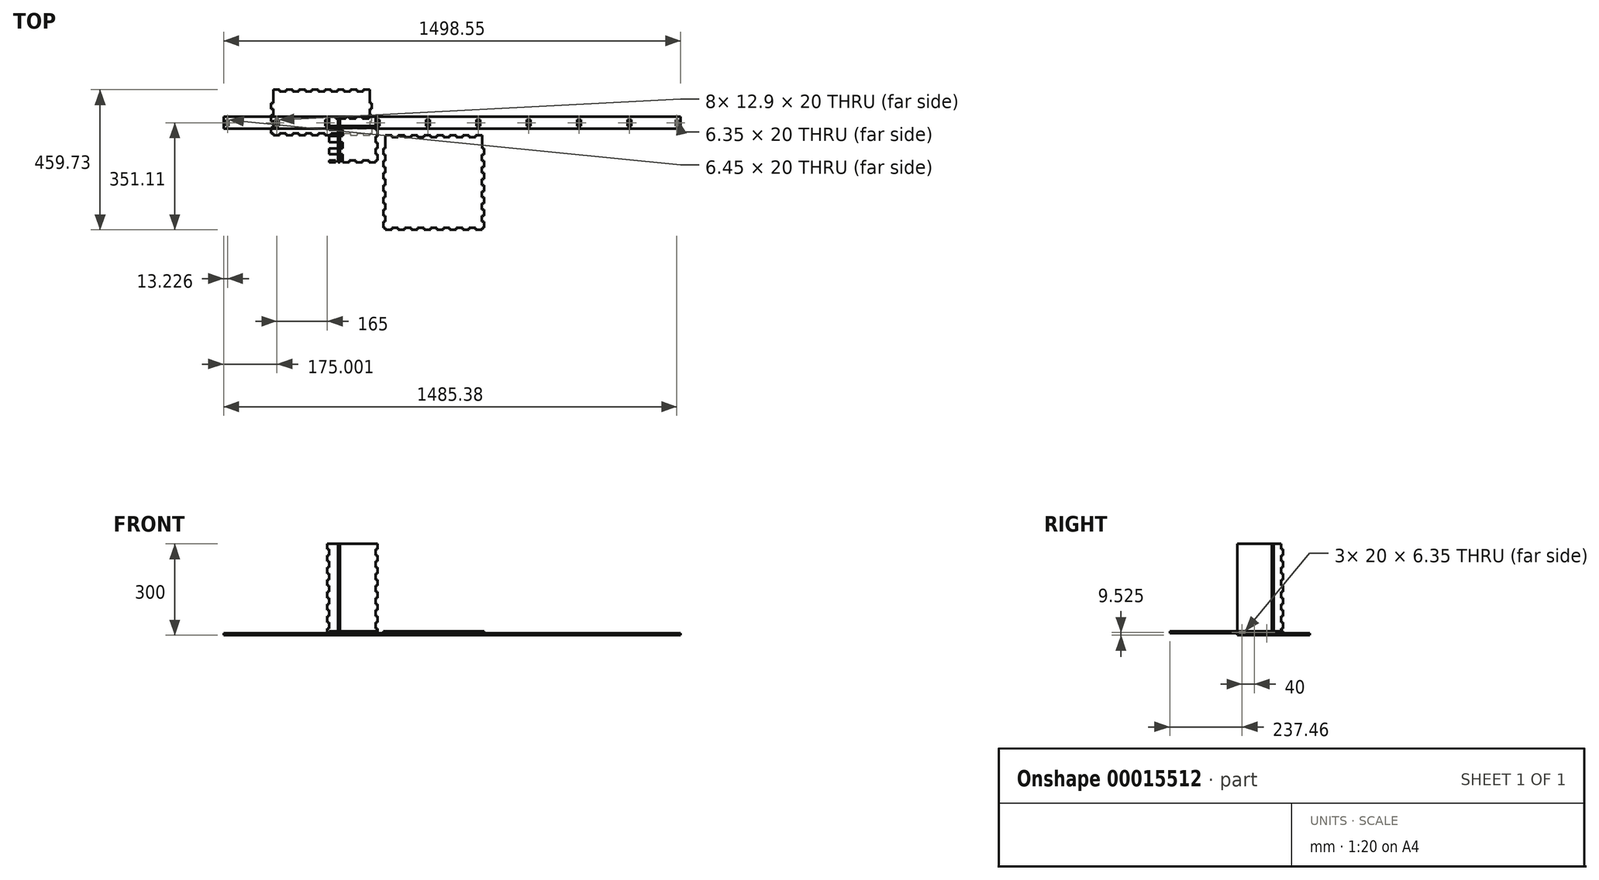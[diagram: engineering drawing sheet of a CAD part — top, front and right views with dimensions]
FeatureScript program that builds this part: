
annotation { "Feature Type Name" : "Feature", "Feature Type Description" : "" }
export const myFeature = defineFeature(function(context is Context, id is Id, definition is map)
    precondition{}
    {
        {
            var Q0;
            Q0=qCreatedBy(makeId("Top.planeOp"),FACE);
            var sketch = newSketch(context, id + "F0", { "sketchPlane" : qUnion([Q0])});
            skLineSegment(sketch, "E0.bottom", {"start": v(-375.58, 30) * mm, "end": v(1122.97, 30) * mm});
            skLineSegment(sketch, "E0.top", {"start": v(-375.58, -10) * mm, "end": v(1122.97, -10) * mm});
            skLineSegment(sketch, "E0.left", {"start": v(-375.58, 30) * mm, "end": v(-375.58, -10) * mm});
            skLineSegment(sketch, "E0.right", {"start": v(1122.97, 30) * mm, "end": v(1122.97, -10) * mm});
            skLineSegment(sketch, "E1.bottom", {"start": v(-207.03, 20) * mm, "end": v(-194.13, 20) * mm});
            skLineSegment(sketch, "E1.top", {"start": v(-207.03, 0) * mm, "end": v(-194.13, 0) * mm});
            skLineSegment(sketch, "E1.left", {"start": v(-207.03, 20) * mm, "end": v(-207.03, 0) * mm});
            skLineSegment(sketch, "E1.right", {"start": v(-194.13, 20) * mm, "end": v(-194.13, 0) * mm});
            skLineSegment(sketch, "E2.1.0.0", {"start": v(-29.13, 20) * mm, "end": v(-29.13, 0) * mm});
            skLineSegment(sketch, "E2.1.0.1", {"start": v(-42.03, 0) * mm, "end": v(-29.13, 0) * mm});
            skLineSegment(sketch, "E2.1.0.2", {"start": v(-42.03, 20) * mm, "end": v(-42.03, 0) * mm});
            skLineSegment(sketch, "E2.1.0.3", {"start": v(-42.03, 20) * mm, "end": v(-29.13, 20) * mm});
            skLineSegment(sketch, "E2.2.0.0", {"start": v(135.87, 20) * mm, "end": v(135.87, 0) * mm});
            skLineSegment(sketch, "E2.2.0.1", {"start": v(122.97, 0) * mm, "end": v(135.87, 0) * mm});
            skLineSegment(sketch, "E2.2.0.2", {"start": v(122.97, 20) * mm, "end": v(122.97, 0) * mm});
            skLineSegment(sketch, "E2.2.0.3", {"start": v(122.97, 20) * mm, "end": v(135.87, 20) * mm});
            skLineSegment(sketch, "E2.3.0.0", {"start": v(300.87, 20) * mm, "end": v(300.87, 0) * mm});
            skLineSegment(sketch, "E2.3.0.1", {"start": v(287.97, 0) * mm, "end": v(300.87, 0) * mm});
            skLineSegment(sketch, "E2.3.0.2", {"start": v(287.97, 20) * mm, "end": v(287.97, 0) * mm});
            skLineSegment(sketch, "E2.3.0.3", {"start": v(287.97, 20) * mm, "end": v(300.87, 20) * mm});
            skLineSegment(sketch, "E2.4.0.0", {"start": v(465.87, 20) * mm, "end": v(465.87, 0) * mm});
            skLineSegment(sketch, "E2.4.0.1", {"start": v(452.97, 0) * mm, "end": v(465.87, 0) * mm});
            skLineSegment(sketch, "E2.4.0.2", {"start": v(452.97, 20) * mm, "end": v(452.97, 0) * mm});
            skLineSegment(sketch, "E2.4.0.3", {"start": v(452.97, 20) * mm, "end": v(465.87, 20) * mm});
            skLineSegment(sketch, "E2.5.0.0", {"start": v(630.87, 20) * mm, "end": v(630.87, 0) * mm});
            skLineSegment(sketch, "E2.5.0.1", {"start": v(617.97, 0) * mm, "end": v(630.87, 0) * mm});
            skLineSegment(sketch, "E2.5.0.2", {"start": v(617.97, 20) * mm, "end": v(617.97, 0) * mm});
            skLineSegment(sketch, "E2.5.0.3", {"start": v(617.97, 20) * mm, "end": v(630.87, 20) * mm});
            skLineSegment(sketch, "E2.6.0.0", {"start": v(795.87, 20) * mm, "end": v(795.87, 0) * mm});
            skLineSegment(sketch, "E2.6.0.1", {"start": v(782.97, 0) * mm, "end": v(795.87, 0) * mm});
            skLineSegment(sketch, "E2.6.0.2", {"start": v(782.97, 20) * mm, "end": v(782.97, 0) * mm});
            skLineSegment(sketch, "E2.6.0.3", {"start": v(782.97, 20) * mm, "end": v(795.87, 20) * mm});
            skLineSegment(sketch, "E2.7.0.0", {"start": v(960.87, 20) * mm, "end": v(960.87, 0) * mm});
            skLineSegment(sketch, "E2.7.0.1", {"start": v(947.97, 0) * mm, "end": v(960.87, 0) * mm});
            skLineSegment(sketch, "E2.7.0.2", {"start": v(947.97, 20) * mm, "end": v(947.97, 0) * mm});
            skLineSegment(sketch, "E2.7.0.3", {"start": v(947.97, 20) * mm, "end": v(960.87, 20) * mm});
            skLineSegment(sketch, "E2.direction1", {"start": v(-194.13, 0) * mm, "end": v(-29.13, 0) * mm, "construction": true});
            skLineSegment(sketch, "E3.top", {"start": v(-365.58, 0) * mm, "end": v(-359.13, 0) * mm});
            skLineSegment(sketch, "E3.right", {"start": v(-359.13, 20) * mm, "end": v(-359.13, 0) * mm});
            skLineSegment(sketch, "E3.bottom", {"start": v(-365.58, 20) * mm, "end": v(-359.13, 20) * mm});
            skLineSegment(sketch, "E3.left", {"start": v(-365.58, 20) * mm, "end": v(-365.58, 0) * mm});
            skLineSegment(sketch, "E4.top", {"start": v(1106.62, 0) * mm, "end": v(1112.97, 0) * mm});
            skLineSegment(sketch, "E4.left", {"start": v(1106.62, 20) * mm, "end": v(1106.62, 0) * mm});
            skLineSegment(sketch, "E4.bottom", {"start": v(1106.62, 20) * mm, "end": v(1112.97, 20) * mm});
            skLineSegment(sketch, "E4.right", {"start": v(1112.97, 20) * mm, "end": v(1112.97, 0) * mm});
            skSolve(sketch);
        }
        {
            var Q0;
            Q0=makeQuery(id+"F0.imprint","IMPRINT",FACE,{"disambiguationData":[TD([[makeQuery(id+"F0.imprint","IMPRINT",EDGE,{"derivedFrom":sQuery(id+"F0.wireOp",EDGE,"E0.bottom")}),-1.0]])]});
            extrude(context, id + "F1", {"entities" : qUnion([Q0]), "depth" : 6.35 * mm});
        }
        {
            var Q0;
            Q0=qCreatedBy(makeId("Right.planeOp"),FACE);
            var sketch = newSketch(context, id + "F2", { "sketchPlane" : qUnion([Q0])});
            skLineSegment(sketch, "E5.bottom", {"start": v(30, 300) * mm, "end": v(-120, 300) * mm});
            skLineSegment(sketch, "E5.left", {"start": v(30, 300) * mm, "end": v(30, 6.35) * mm});
            skLineSegment(sketch, "E5.right", {"start": v(-120, 300) * mm, "end": v(-120, 0) * mm});
            skLineSegment(sketch, "E6.0", {"start": v(30, 6.35) * mm, "end": v(20, 6.35) * mm});
            skLineSegment(sketch, "E6.1", {"start": v(-10.2, 6.35) * mm, "end": v(-10.2, 0) * mm});
            skPoint(sketch, "E7.0", {"position": v(20, 0) * mm});
            skLineSegment(sketch, "E8", {"start": v(20, 0) * mm, "end": v(20, 6.35) * mm});
            skLineSegment(sketch, "E9.trimOffspring", {"start": v(0, 6.35) * mm, "end": v(-10.2, 6.35) * mm});
            skLineSegment(sketch, "E10", {"start": v(-10.2, 0) * mm, "end": v(-120, 0) * mm});
            skLineSegment(sketch, "E11", {"start": v(20, 0) * mm, "end": v(0, 0) * mm});
            skLineSegment(sketch, "E12", {"start": v(0, 0) * mm, "end": v(0, 6.35) * mm});
            skSolve(sketch);
        }
        {
            var Q0;
            Q0 = qSketchRegion(id + "F2", true);
            extrude(context, id + "F3", {"entities" : qUnion([Q0]), "depth" : 6.35 * mm});
        }
        {
            var Q0;
            Q0=makeQuery(id+"F1.opExtrude","CAP_FACE",FACE,{"disambiguationData":[OSD([sQuery(id+"F0.wireOp",EDGE,"E0.bottom"),sQuery(id+"F0.wireOp",EDGE,"E0.top"),sQuery(id+"F0.wireOp",EDGE,"E0.left"),sQuery(id+"F0.wireOp",EDGE,"E0.right"),sQuery(id+"F0.wireOp",EDGE,"E1.bottom"),sQuery(id+"F0.wireOp",EDGE,"E1.top"),sQuery(id+"F0.wireOp",EDGE,"E1.left"),sQuery(id+"F0.wireOp",EDGE,"E1.right"),sQuery(id+"F0.wireOp",EDGE,"E2.1.0.0"),sQuery(id+"F0.wireOp",EDGE,"E2.1.0.1"),sQuery(id+"F0.wireOp",EDGE,"E2.1.0.2"),sQuery(id+"F0.wireOp",EDGE,"E2.1.0.3"),sQuery(id+"F0.wireOp",EDGE,"E2.2.0.0"),sQuery(id+"F0.wireOp",EDGE,"E2.2.0.1"),sQuery(id+"F0.wireOp",EDGE,"E2.2.0.2"),sQuery(id+"F0.wireOp",EDGE,"E2.2.0.3"),sQuery(id+"F0.wireOp",EDGE,"E2.3.0.0"),sQuery(id+"F0.wireOp",EDGE,"E2.3.0.1"),sQuery(id+"F0.wireOp",EDGE,"E2.3.0.2"),sQuery(id+"F0.wireOp",EDGE,"E2.3.0.3"),sQuery(id+"F0.wireOp",EDGE,"E2.4.0.0"),sQuery(id+"F0.wireOp",EDGE,"E2.4.0.1"),sQuery(id+"F0.wireOp",EDGE,"E2.4.0.2"),sQuery(id+"F0.wireOp",EDGE,"E2.4.0.3"),sQuery(id+"F0.wireOp",EDGE,"E2.5.0.0"),sQuery(id+"F0.wireOp",EDGE,"E2.5.0.1"),sQuery(id+"F0.wireOp",EDGE,"E2.5.0.2"),sQuery(id+"F0.wireOp",EDGE,"E2.5.0.3"),sQuery(id+"F0.wireOp",EDGE,"E2.6.0.0"),sQuery(id+"F0.wireOp",EDGE,"E2.6.0.1"),sQuery(id+"F0.wireOp",EDGE,"E2.6.0.2"),sQuery(id+"F0.wireOp",EDGE,"E2.6.0.3"),sQuery(id+"F0.wireOp",EDGE,"E2.7.0.0"),sQuery(id+"F0.wireOp",EDGE,"E2.7.0.1"),sQuery(id+"F0.wireOp",EDGE,"E2.7.0.2"),sQuery(id+"F0.wireOp",EDGE,"E2.7.0.3"),sQuery(id+"F0.wireOp",EDGE,"E3.top"),sQuery(id+"F0.wireOp",EDGE,"E3.right"),sQuery(id+"F0.wireOp",EDGE,"E3.bottom"),sQuery(id+"F0.wireOp",EDGE,"E3.left"),sQuery(id+"F0.wireOp",EDGE,"E4.top"),sQuery(id+"F0.wireOp",EDGE,"E4.left"),sQuery(id+"F0.wireOp",EDGE,"E4.bottom"),sQuery(id+"F0.wireOp",EDGE,"E4.right")])],"isStart":false});
            var sketch = newSketch(context, id + "F4", { "sketchPlane" : qUnion([Q0])});
            skLineSegment(sketch, "E13.bottom", {"start": v(-29.13, 30) * mm, "end": v(-7.43, 30) * mm});
            skLineSegment(sketch, "E13.top", {"start": v(-29.13, -120) * mm, "end": v(-7.43, -120) * mm});
            skLineSegment(sketch, "E13.left", {"start": v(-35.68, -13.65) * mm, "end": v(-35.68, -33.65) * mm});
            skLineSegment(sketch, "E13.right", {"start": v(129.52, -13.65) * mm, "end": v(129.52, -35) * mm});
            skLineSegment(sketch, "E14.0", {"start": v(-29.13, 30) * mm, "end": v(-29.13, -13.65) * mm});
            skPoint(sketch, "E15.orphan", {"position": v(-29.13, 20) * mm});
            skLineSegment(sketch, "E16.0", {"start": v(-35.68, -13.65) * mm, "end": v(-29.13, -13.65) * mm});
            skPoint(sketch, "E17.orphan", {"position": v(-29.13, 0) * mm});
            skPoint(sketch, "E18.orphan", {"position": v(-375.58, -10) * mm});
            skPoint(sketch, "E19.orphan", {"position": v(1122.97, -10) * mm});
            skLineSegment(sketch, "E20", {"start": v(-29.13, -73.65) * mm, "end": v(-35.68, -73.65) * mm});
            skLineSegment(sketch, "E21", {"start": v(-29.13, -93.65) * mm, "end": v(-35.68, -93.65) * mm});
            skLineSegment(sketch, "E22", {"start": v(-7.43, -113.65) * mm, "end": v(14.27, -113.65) * mm});
            skLineSegment(sketch, "E23.0.1.0", {"start": v(-29.13, -53.65) * mm, "end": v(-35.68, -53.65) * mm});
            skLineSegment(sketch, "E23.0.2.0", {"start": v(-29.13, -33.65) * mm, "end": v(-35.68, -33.65) * mm});
            skLineSegment(sketch, "E23.direction1", {"start": v(-35.68, -73.65) * mm, "end": v(-29.13, -73.65) * mm, "construction": true});
            skLineSegment(sketch, "E23.direction2", {"start": v(-35.68, -73.65) * mm, "end": v(-35.68, -53.65) * mm, "construction": true});
            skLineSegment(sketch, "E24.trimOffspring", {"start": v(-29.13, -33.65) * mm, "end": v(-29.13, -53.65) * mm});
            skLineSegment(sketch, "E25.trimOffspring", {"start": v(-35.68, -53.65) * mm, "end": v(-35.68, -73.65) * mm});
            skLineSegment(sketch, "E26.trimOffspring", {"start": v(-29.13, -73.65) * mm, "end": v(-29.13, -93.65) * mm});
            skLineSegment(sketch, "E27", {"start": v(-29.13, -113.65) * mm, "end": v(-35.68, -113.65) * mm});
            skLineSegment(sketch, "E28.trimOffspring", {"start": v(-35.68, -93.65) * mm, "end": v(-35.68, -113.65) * mm});
            skLineSegment(sketch, "E29.trimOffspring", {"start": v(-29.13, -113.65) * mm, "end": v(-29.13, -120) * mm});
            skLineSegment(sketch, "E30.MirrorCS", {"start": v(129.52, -73.65) * mm, "end": v(129.52, -55) * mm});
            skLineSegment(sketch, "E31.MirrorCS", {"start": v(129.52, -93.65) * mm, "end": v(129.52, -113.65) * mm});
            skLineSegment(sketch, "E32.MirrorCS", {"start": v(129.52, -55) * mm, "end": v(129.52, -73.65) * mm});
            skLineSegment(sketch, "E33.MirrorCS", {"start": v(122.97, -73.65) * mm, "end": v(122.97, -93.65) * mm});
            skLineSegment(sketch, "E34.MirrorCS", {"start": v(122.97, -113.65) * mm, "end": v(129.52, -113.65) * mm});
            skLineSegment(sketch, "E35.MirrorCS", {"start": v(122.97, -35) * mm, "end": v(122.97, -55) * mm});
            skPoint(sketch, "E36.MirrorP", {"position": v(122.97, 0) * mm});
            skLineSegment(sketch, "E37.MirrorCS", {"start": v(122.97, -55) * mm, "end": v(129.52, -55) * mm});
            skLineSegment(sketch, "E38.MirrorCS", {"start": v(122.97, -35) * mm, "end": v(129.52, -35) * mm});
            skLineSegment(sketch, "E39.MirrorCS", {"start": v(122.97, -113.65) * mm, "end": v(122.97, -120) * mm});
            skLineSegment(sketch, "E40.MirrorCS", {"start": v(122.97, -73.65) * mm, "end": v(129.52, -73.65) * mm});
            skLineSegment(sketch, "E41.MirrorCS", {"start": v(122.97, -93.65) * mm, "end": v(129.52, -93.65) * mm});
            skLineSegment(sketch, "E42.MirrorCS", {"start": v(122.97, 30) * mm, "end": v(122.97, -13.65) * mm});
            skLineSegment(sketch, "E43.MirrorCS", {"start": v(122.97, 30) * mm, "end": v(101.07, 30) * mm});
            skPoint(sketch, "E44.MirrorP", {"position": v(122.97, 20) * mm});
            skPoint(sketch, "E45.orphan", {"position": v(129.52, 30) * mm});
            skLineSegment(sketch, "E46", {"start": v(-7.43, -113.65) * mm, "end": v(-7.43, -120) * mm});
            skLineSegment(sketch, "E47.1.0.0", {"start": v(14.27, -113.65) * mm, "end": v(14.27, -120) * mm});
            skLineSegment(sketch, "E47.2.0.0", {"start": v(35.97, -113.65) * mm, "end": v(35.97, -120) * mm});
            skLineSegment(sketch, "E47.3.0.0", {"start": v(57.67, -113.65) * mm, "end": v(57.67, -120) * mm});
            skLineSegment(sketch, "E47.4.0.0", {"start": v(79.37, -113.65) * mm, "end": v(79.37, -120) * mm});
            skLineSegment(sketch, "E47.5.0.0", {"start": v(101.07, -113.65) * mm, "end": v(101.07, -120) * mm});
            skLineSegment(sketch, "E47.direction1", {"start": v(-3.78, -120) * mm, "end": v(17.92, -120) * mm, "construction": true});
            skLineSegment(sketch, "E48.trimOffspring", {"start": v(14.27, -120) * mm, "end": v(35.97, -120) * mm});
            skLineSegment(sketch, "E49", {"start": v(101.07, -120) * mm, "end": v(122.97, -120) * mm});
            skLineSegment(sketch, "E50", {"start": v(35.97, -113.65) * mm, "end": v(57.67, -113.65) * mm});
            skLineSegment(sketch, "E51", {"start": v(79.37, -113.65) * mm, "end": v(101.07, -113.65) * mm});
            skLineSegment(sketch, "E52", {"start": v(57.67, -120) * mm, "end": v(79.37, -120) * mm});
            skLineSegment(sketch, "E53.MirrorCS", {"start": v(35.97, 23.65) * mm, "end": v(35.97, 30) * mm});
            skLineSegment(sketch, "E54.MirrorCS", {"start": v(122.97, 23.65) * mm, "end": v(122.97, 30) * mm});
            skLineSegment(sketch, "E55.MirrorCS", {"start": v(101.07, 30) * mm, "end": v(122.97, 30) * mm});
            skLineSegment(sketch, "E56.MirrorCS", {"start": v(14.27, 23.65) * mm, "end": v(14.27, 30) * mm});
            skLineSegment(sketch, "E57.MirrorCS", {"start": v(57.67, 23.65) * mm, "end": v(57.67, 30) * mm});
            skLineSegment(sketch, "E58.MirrorCS", {"start": v(14.27, 30) * mm, "end": v(35.97, 30) * mm});
            skLineSegment(sketch, "E59.MirrorCS", {"start": v(79.37, 23.65) * mm, "end": v(101.07, 23.65) * mm});
            skLineSegment(sketch, "E60.MirrorCS", {"start": v(35.97, 23.65) * mm, "end": v(57.67, 23.65) * mm});
            skLineSegment(sketch, "E61.MirrorCS", {"start": v(14.27, 30) * mm, "end": v(17.92, 30) * mm});
            skLineSegment(sketch, "E62.MirrorCS", {"start": v(-29.13, 23.65) * mm, "end": v(-29.13, 30) * mm});
            skLineSegment(sketch, "E63.MirrorCS", {"start": v(57.67, 30) * mm, "end": v(79.37, 30) * mm});
            skLineSegment(sketch, "E64.MirrorCS", {"start": v(-7.43, 23.65) * mm, "end": v(-7.43, 30) * mm});
            skLineSegment(sketch, "E65.MirrorCS", {"start": v(-7.43, 23.65) * mm, "end": v(14.27, 23.65) * mm});
            skLineSegment(sketch, "E66.MirrorCS", {"start": v(101.07, 23.65) * mm, "end": v(101.07, 30) * mm});
            skLineSegment(sketch, "E67.MirrorCS", {"start": v(79.37, 23.65) * mm, "end": v(79.37, 30) * mm});
            skLineSegment(sketch, "E68.trimOffspring", {"start": v(-7.43, 30) * mm, "end": v(-29.13, 30) * mm});
            skLineSegment(sketch, "E69.trimOffspring", {"start": v(35.97, 30) * mm, "end": v(14.27, 30) * mm});
            skLineSegment(sketch, "E70.trimOffspring", {"start": v(79.37, 30) * mm, "end": v(57.67, 30) * mm});
            skLineSegment(sketch, "E71.trimOffspring", {"start": v(129.52, -13.65) * mm, "end": v(129.52, -33.65) * mm});
            skLineSegment(sketch, "E72.trimOffspring", {"start": v(122.97, -13.65) * mm, "end": v(129.52, -13.65) * mm});
            skSolve(sketch);
        }
        {
            var Q0;
            Q0 = qSketchRegion(id + "F4", true);
            extrude(context, id + "F5", {"entities" : qUnion([Q0]), "depth" : 6.35 * mm});
        }
        {
            var Q0;
            Q0=makeQuery(id+"F5.opExtrude","SWEPT_FACE",FACE,{"disambiguationData":[OSD([sQuery(id+"F4.wireOp",EDGE,"E28.trimOffspring")])]});
            var sketch = newSketch(context, id + "F6", { "sketchPlane" : qUnion([Q0])});
            skLineSegment(sketch, "E73.0.0", {"start": v(13.65, 6.35) * mm, "end": v(33.65, 6.35) * mm});
            skLineSegment(sketch, "E73.0.1", {"start": v(33.65, 6.35) * mm, "end": v(33.65, 12.7) * mm});
            skLineSegment(sketch, "E73.0.2", {"start": v(33.65, 12.7) * mm, "end": v(13.65, 12.7) * mm});
            skLineSegment(sketch, "E73.0.3", {"start": v(13.65, 12.7) * mm, "end": v(13.65, 6.35) * mm});
            skLineSegment(sketch, "E74.0.0", {"start": v(53.65, 6.35) * mm, "end": v(73.65, 6.35) * mm});
            skLineSegment(sketch, "E74.0.1", {"start": v(73.65, 6.35) * mm, "end": v(73.65, 12.7) * mm});
            skLineSegment(sketch, "E74.0.2", {"start": v(73.65, 12.7) * mm, "end": v(53.65, 12.7) * mm});
            skLineSegment(sketch, "E74.0.3", {"start": v(53.65, 12.7) * mm, "end": v(53.65, 6.35) * mm});
            skLineSegment(sketch, "E75.0.0", {"start": v(93.65, 6.35) * mm, "end": v(113.65, 6.35) * mm});
            skLineSegment(sketch, "E75.0.1", {"start": v(113.65, 6.35) * mm, "end": v(113.65, 12.7) * mm});
            skLineSegment(sketch, "E75.0.2", {"start": v(113.65, 12.7) * mm, "end": v(93.65, 12.7) * mm});
            skLineSegment(sketch, "E75.0.3", {"start": v(93.65, 12.7) * mm, "end": v(93.65, 6.35) * mm});
            skSolve(sketch);
        }
        {
            var Q0;
            Q0 = qSketchRegion(id + "F6", true);
            extrude(context, id + "F7", {"entities" : qUnion([Q0]), "operationType" : NewBodyOperationType.REMOVE, "oppositeDirection" : true, "depth" : 50 * mm});
        }
        {
            var Q0;
            Q0=qCreatedBy(makeId("Front.planeOp"),FACE);
            var sketch = newSketch(context, id + "F8", { "sketchPlane" : qUnion([Q0])});
            skLineSegment(sketch, "E76.0.1", {"start": v(129.52, 0) * mm, "end": v(129.52, 300) * mm});
            skLineSegment(sketch, "E77.0.3", {"start": v(-35.68, 300) * mm, "end": v(-35.68, 0) * mm});
            skLineSegment(sketch, "E78.0.1", {"start": v(-45.56, 0) * mm, "end": v(140.5, 0) * mm});
            skLineSegment(sketch, "E78.0.3", {"start": v(336.52, 300) * mm, "end": v(-42.2, 300) * mm});
            skLineSegment(sketch, "E79.0.0", {"start": v(-35.68, 6.35) * mm, "end": v(101.07, 6.35) * mm});
            skLineSegment(sketch, "E79.0.1", {"start": v(-7.43, 6.35) * mm, "end": v(-7.43, 12.7) * mm});
            skLineSegment(sketch, "E79.0.2", {"start": v(-7.43, 12.7) * mm, "end": v(-29.13, 12.7) * mm});
            skLineSegment(sketch, "E79.0.3", {"start": v(-29.13, 12.7) * mm, "end": v(-29.13, 6.35) * mm});
            skLineSegment(sketch, "E80.0.0", {"start": v(14.27, 6.35) * mm, "end": v(35.97, 6.35) * mm});
            skLineSegment(sketch, "E80.0.1", {"start": v(35.97, 6.35) * mm, "end": v(35.97, 12.7) * mm});
            skLineSegment(sketch, "E80.0.2", {"start": v(35.97, 12.7) * mm, "end": v(14.27, 12.7) * mm});
            skLineSegment(sketch, "E80.0.3", {"start": v(14.27, 12.7) * mm, "end": v(14.27, 6.35) * mm});
            skLineSegment(sketch, "E81.0.0", {"start": v(57.67, 6.35) * mm, "end": v(79.37, 6.35) * mm});
            skLineSegment(sketch, "E81.0.1", {"start": v(79.37, 6.35) * mm, "end": v(79.37, 12.7) * mm});
            skLineSegment(sketch, "E81.0.2", {"start": v(79.37, 12.7) * mm, "end": v(57.67, 12.7) * mm});
            skLineSegment(sketch, "E81.0.3", {"start": v(57.67, 12.7) * mm, "end": v(57.67, 6.35) * mm});
            skLineSegment(sketch, "E82.0.0", {"start": v(101.07, 6.35) * mm, "end": v(129.52, 6.35) * mm});
            skLineSegment(sketch, "E82.0.1", {"start": v(122.97, 6.35) * mm, "end": v(122.97, 12.7) * mm});
            skLineSegment(sketch, "E82.0.2", {"start": v(122.97, 12.7) * mm, "end": v(101.07, 12.7) * mm});
            skLineSegment(sketch, "E82.0.3", {"start": v(101.07, 12.7) * mm, "end": v(101.07, 6.35) * mm});
            skLineSegment(sketch, "E83", {"start": v(-35.68, 22.7) * mm, "end": v(-29.33, 22.7) * mm});
            skLineSegment(sketch, "E84", {"start": v(-35.68, 42.7) * mm, "end": v(-29.33, 42.7) * mm});
            skLineSegment(sketch, "E85", {"start": v(-29.33, 42.7) * mm, "end": v(-29.33, 22.7) * mm});
            skLineSegment(sketch, "E86", {"start": v(123.17, 42.7) * mm, "end": v(123.17, 22.7) * mm});
            skLineSegment(sketch, "E87.trimOffspring", {"start": v(123.17, 42.7) * mm, "end": v(129.52, 42.7) * mm});
            skLineSegment(sketch, "E88.trimOffspring", {"start": v(123.17, 22.7) * mm, "end": v(129.52, 22.7) * mm});
            skLineSegment(sketch, "E89.0.1.0", {"start": v(-29.33, 82.7) * mm, "end": v(-29.33, 62.7) * mm});
            skLineSegment(sketch, "E89.0.1.1", {"start": v(-35.68, 62.7) * mm, "end": v(-29.33, 62.7) * mm});
            skLineSegment(sketch, "E89.0.1.2", {"start": v(-35.68, 82.7) * mm, "end": v(-29.33, 82.7) * mm});
            skLineSegment(sketch, "E89.0.1.3", {"start": v(123.17, 82.7) * mm, "end": v(129.52, 82.7) * mm});
            skLineSegment(sketch, "E89.0.1.4", {"start": v(123.17, 82.7) * mm, "end": v(123.17, 62.7) * mm});
            skLineSegment(sketch, "E89.0.1.5", {"start": v(123.17, 62.7) * mm, "end": v(129.52, 62.7) * mm});
            skLineSegment(sketch, "E89.0.2.0", {"start": v(-29.33, 122.7) * mm, "end": v(-29.33, 102.7) * mm});
            skLineSegment(sketch, "E89.0.2.1", {"start": v(-35.68, 102.7) * mm, "end": v(-29.33, 102.7) * mm});
            skLineSegment(sketch, "E89.0.2.2", {"start": v(-35.68, 122.7) * mm, "end": v(-29.33, 122.7) * mm});
            skLineSegment(sketch, "E89.0.2.3", {"start": v(123.17, 122.7) * mm, "end": v(129.52, 122.7) * mm});
            skLineSegment(sketch, "E89.0.2.4", {"start": v(123.17, 122.7) * mm, "end": v(123.17, 102.7) * mm});
            skLineSegment(sketch, "E89.0.2.5", {"start": v(123.17, 102.7) * mm, "end": v(129.52, 102.7) * mm});
            skLineSegment(sketch, "E89.0.3.0", {"start": v(-29.33, 162.7) * mm, "end": v(-29.33, 142.7) * mm});
            skLineSegment(sketch, "E89.0.3.1", {"start": v(-35.68, 142.7) * mm, "end": v(-29.33, 142.7) * mm});
            skLineSegment(sketch, "E89.0.3.2", {"start": v(-35.68, 162.7) * mm, "end": v(-29.33, 162.7) * mm});
            skLineSegment(sketch, "E89.0.3.3", {"start": v(123.17, 162.7) * mm, "end": v(129.52, 162.7) * mm});
            skLineSegment(sketch, "E89.0.3.4", {"start": v(123.17, 162.7) * mm, "end": v(123.17, 142.7) * mm});
            skLineSegment(sketch, "E89.0.3.5", {"start": v(123.17, 142.7) * mm, "end": v(129.52, 142.7) * mm});
            skLineSegment(sketch, "E89.0.4.0", {"start": v(-29.33, 202.7) * mm, "end": v(-29.33, 182.7) * mm});
            skLineSegment(sketch, "E89.0.4.1", {"start": v(-35.68, 182.7) * mm, "end": v(-29.33, 182.7) * mm});
            skLineSegment(sketch, "E89.0.4.2", {"start": v(-35.68, 202.7) * mm, "end": v(-29.33, 202.7) * mm});
            skLineSegment(sketch, "E89.0.4.3", {"start": v(123.17, 202.7) * mm, "end": v(129.52, 202.7) * mm});
            skLineSegment(sketch, "E89.0.4.4", {"start": v(123.17, 202.7) * mm, "end": v(123.17, 182.7) * mm});
            skLineSegment(sketch, "E89.0.4.5", {"start": v(123.17, 182.7) * mm, "end": v(129.52, 182.7) * mm});
            skLineSegment(sketch, "E89.0.5.0", {"start": v(-29.33, 242.7) * mm, "end": v(-29.33, 222.7) * mm});
            skLineSegment(sketch, "E89.0.5.1", {"start": v(-35.68, 222.7) * mm, "end": v(-29.33, 222.7) * mm});
            skLineSegment(sketch, "E89.0.5.2", {"start": v(-35.68, 242.7) * mm, "end": v(-29.33, 242.7) * mm});
            skLineSegment(sketch, "E89.0.5.3", {"start": v(123.17, 242.7) * mm, "end": v(129.52, 242.7) * mm});
            skLineSegment(sketch, "E89.0.5.4", {"start": v(123.17, 242.7) * mm, "end": v(123.17, 222.7) * mm});
            skLineSegment(sketch, "E89.0.5.5", {"start": v(123.17, 222.7) * mm, "end": v(129.52, 222.7) * mm});
            skLineSegment(sketch, "E89.0.6.0", {"start": v(-29.33, 282.7) * mm, "end": v(-29.33, 262.7) * mm});
            skLineSegment(sketch, "E89.0.6.1", {"start": v(-35.68, 262.7) * mm, "end": v(-29.33, 262.7) * mm});
            skLineSegment(sketch, "E89.0.6.2", {"start": v(-35.68, 282.7) * mm, "end": v(-29.33, 282.7) * mm});
            skLineSegment(sketch, "E89.0.6.3", {"start": v(123.17, 282.7) * mm, "end": v(129.52, 282.7) * mm});
            skLineSegment(sketch, "E89.0.6.4", {"start": v(123.17, 282.7) * mm, "end": v(123.17, 262.7) * mm});
            skLineSegment(sketch, "E89.0.6.5", {"start": v(123.17, 262.7) * mm, "end": v(129.52, 262.7) * mm});
            skLineSegment(sketch, "E89.direction1", {"start": v(-29.33, 22.7) * mm, "end": v(-4.33, 22.7) * mm, "construction": true});
            skLineSegment(sketch, "E89.direction2", {"start": v(-29.33, 22.7) * mm, "end": v(-29.33, 62.7) * mm, "construction": true});
            skSolve(sketch);
        }
        {
            var Q0;
            {var subQ39=sQuery(id+"F8.wireOp",EDGE,"E79.0.1");Q0=makeQuery(id+"F8.imprint","IMPRINT",FACE,{"disambiguationData":[TD([[makeQuery(id+"F8.imprint","IMPRINT",EDGE,{"derivedFrom":subQ39}),-1.0]])]});}
            extrude(context, id + "F9", {"entities" : qUnion([Q0]), "depth" : 6.35 * mm});
        }
        {
            var Q0;
            Q0=qCreatedBy(makeId("Right.planeOp"),FACE);
            var sketch = newSketch(context, id + "F10", { "sketchPlane" : qUnion([Q0])});
            skLineSegment(sketch, "E90.0.0", {"start": v(30, 22.7) * mm, "end": v(30, 6.35) * mm});
            skLineSegment(sketch, "E90.0.1", {"start": v(30, 6.35) * mm, "end": v(23.65, 6.35) * mm});
            skLineSegment(sketch, "E90.0.2", {"start": v(23.65, 6.35) * mm, "end": v(23.65, 22.7) * mm});
            skLineSegment(sketch, "E90.0.3", {"start": v(23.65, 22.7) * mm, "end": v(30, 22.7) * mm});
            skLineSegment(sketch, "E91.0.0", {"start": v(30, 62.7) * mm, "end": v(30, 42.7) * mm});
            skLineSegment(sketch, "E91.0.1", {"start": v(30, 42.7) * mm, "end": v(23.65, 42.7) * mm});
            skLineSegment(sketch, "E91.0.2", {"start": v(23.65, 42.7) * mm, "end": v(23.65, 62.7) * mm});
            skLineSegment(sketch, "E91.0.3", {"start": v(23.65, 62.7) * mm, "end": v(30, 62.7) * mm});
            skLineSegment(sketch, "E92.0.1.0", {"start": v(23.65, 82.7) * mm, "end": v(23.65, 102.7) * mm});
            skLineSegment(sketch, "E92.0.1.1", {"start": v(30, 82.7) * mm, "end": v(23.65, 82.7) * mm});
            skLineSegment(sketch, "E92.0.1.2", {"start": v(30, 102.7) * mm, "end": v(30, 82.7) * mm});
            skLineSegment(sketch, "E92.0.1.3", {"start": v(23.65, 102.7) * mm, "end": v(30, 102.7) * mm});
            skLineSegment(sketch, "E92.0.2.0", {"start": v(23.65, 122.7) * mm, "end": v(23.65, 142.7) * mm});
            skLineSegment(sketch, "E92.0.2.1", {"start": v(30, 122.7) * mm, "end": v(23.65, 122.7) * mm});
            skLineSegment(sketch, "E92.0.2.2", {"start": v(30, 142.7) * mm, "end": v(30, 122.7) * mm});
            skLineSegment(sketch, "E92.0.2.3", {"start": v(23.65, 142.7) * mm, "end": v(30, 142.7) * mm});
            skLineSegment(sketch, "E92.0.3.0", {"start": v(23.65, 162.7) * mm, "end": v(23.65, 182.7) * mm});
            skLineSegment(sketch, "E92.0.3.1", {"start": v(30, 162.7) * mm, "end": v(23.65, 162.7) * mm});
            skLineSegment(sketch, "E92.0.3.2", {"start": v(30, 182.7) * mm, "end": v(30, 162.7) * mm});
            skLineSegment(sketch, "E92.0.3.3", {"start": v(23.65, 182.7) * mm, "end": v(30, 182.7) * mm});
            skLineSegment(sketch, "E92.0.4.0", {"start": v(23.65, 202.7) * mm, "end": v(23.65, 222.7) * mm});
            skLineSegment(sketch, "E92.0.4.1", {"start": v(30, 202.7) * mm, "end": v(23.65, 202.7) * mm});
            skLineSegment(sketch, "E92.0.4.2", {"start": v(30, 222.7) * mm, "end": v(30, 202.7) * mm});
            skLineSegment(sketch, "E92.0.4.3", {"start": v(23.65, 222.7) * mm, "end": v(30, 222.7) * mm});
            skLineSegment(sketch, "E92.0.5.0", {"start": v(23.65, 242.7) * mm, "end": v(23.65, 262.7) * mm});
            skLineSegment(sketch, "E92.0.5.1", {"start": v(30, 242.7) * mm, "end": v(23.65, 242.7) * mm});
            skLineSegment(sketch, "E92.0.5.2", {"start": v(30, 262.7) * mm, "end": v(30, 242.7) * mm});
            skLineSegment(sketch, "E92.0.5.3", {"start": v(23.65, 262.7) * mm, "end": v(30, 262.7) * mm});
            skLineSegment(sketch, "E92.0.6.0", {"start": v(23.65, 282.7) * mm, "end": v(23.65, 302.7) * mm});
            skLineSegment(sketch, "E92.0.6.1", {"start": v(30, 282.7) * mm, "end": v(23.65, 282.7) * mm});
            skLineSegment(sketch, "E92.0.6.2", {"start": v(30, 302.7) * mm, "end": v(30, 282.7) * mm});
            skLineSegment(sketch, "E92.0.6.3", {"start": v(23.65, 302.7) * mm, "end": v(30, 302.7) * mm});
            skLineSegment(sketch, "E92.direction1", {"start": v(23.65, 42.7) * mm, "end": v(48.65, 42.7) * mm, "construction": true});
            skLineSegment(sketch, "E92.direction2", {"start": v(23.65, 42.7) * mm, "end": v(23.65, 82.7) * mm, "construction": true});
            skSolve(sketch);
        }
        {
            var Q0;
            Q0=makeQuery(id+"F10.imprint","IMPRINT",FACE,{"disambiguationData":[TD([[makeQuery(id+"F10.imprint","IMPRINT",EDGE,{"derivedFrom":sQuery(id+"F10.wireOp",EDGE,"E92.0.6.0")}),-1.0]])]});
            var Q1;
            Q1=makeQuery(id+"F10.imprint","IMPRINT",FACE,{"disambiguationData":[TD([[makeQuery(id+"F10.imprint","IMPRINT",EDGE,{"derivedFrom":sQuery(id+"F10.wireOp",EDGE,"E92.0.5.0")}),-1.0]])]});
            var Q2;
            Q2=makeQuery(id+"F10.imprint","IMPRINT",FACE,{"disambiguationData":[TD([[makeQuery(id+"F10.imprint","IMPRINT",EDGE,{"derivedFrom":sQuery(id+"F10.wireOp",EDGE,"E92.0.4.0")}),-1.0]])]});
            var Q3;
            Q3=makeQuery(id+"F10.imprint","IMPRINT",FACE,{"disambiguationData":[TD([[makeQuery(id+"F10.imprint","IMPRINT",EDGE,{"derivedFrom":sQuery(id+"F10.wireOp",EDGE,"E92.0.3.0")}),-1.0]])]});
            var Q4;
            Q4=makeQuery(id+"F10.imprint","IMPRINT",FACE,{"disambiguationData":[TD([[makeQuery(id+"F10.imprint","IMPRINT",EDGE,{"derivedFrom":sQuery(id+"F10.wireOp",EDGE,"E92.0.2.0")}),-1.0]])]});
            var Q5;
            Q5=makeQuery(id+"F10.imprint","IMPRINT",FACE,{"disambiguationData":[TD([[makeQuery(id+"F10.imprint","IMPRINT",EDGE,{"derivedFrom":sQuery(id+"F10.wireOp",EDGE,"E92.0.1.0")}),-1.0]])]});
            var Q6;
            Q6=makeQuery(id+"F10.imprint","IMPRINT",FACE,{"disambiguationData":[TD([[makeQuery(id+"F10.imprint","IMPRINT",EDGE,{"derivedFrom":sQuery(id+"F10.wireOp",EDGE,"E91.0.0")}),-1.0]])]});
            var Q7;
            Q7=makeQuery(id+"F10.imprint","IMPRINT",FACE,{"disambiguationData":[TD([[makeQuery(id+"F10.imprint","IMPRINT",EDGE,{"derivedFrom":sQuery(id+"F10.wireOp",EDGE,"E90.0.0")}),-1.0]])]});
            extrude(context, id + "F11", {"entities" : qUnion([Q0, Q1, Q2, Q3, Q4, Q5, Q6, Q7]), "operationType" : NewBodyOperationType.REMOVE, "depth" : 25 * mm});
        }
        {
            var Q0;
            Q0=qCreatedBy(makeId("Top.planeOp"),FACE);
            var sketch = newSketch(context, id + "F12", { "sketchPlane" : qUnion([Q0])});
            skLineSegment(sketch, "E93.bottom", {"start": v(-212.8, 118.62) * mm, "end": v(-191.1, 118.62) * mm});
            skLineSegment(sketch, "E93.top", {"start": v(-212.8, -31.38) * mm, "end": v(-191.7, -31.38) * mm});
            skLineSegment(sketch, "E93.left", {"start": v(-219.36, 74.97) * mm, "end": v(-219.36, 54.97) * mm});
            skLineSegment(sketch, "E93.right", {"start": v(110.24, 74.97) * mm, "end": v(110.24, 54.97) * mm});
            skLineSegment(sketch, "E94.0", {"start": v(-212.8, 118.62) * mm, "end": v(-212.8, 74.97) * mm});
            skPoint(sketch, "E95.orphan", {"position": v(-212.8, 108.62) * mm});
            skLineSegment(sketch, "E96.0", {"start": v(-219.36, 74.97) * mm, "end": v(-212.8, 74.97) * mm});
            skPoint(sketch, "E97.orphan", {"position": v(-212.8, 88.62) * mm});
            skPoint(sketch, "E98.orphan", {"position": v(-559.26, 74.97) * mm});
            skPoint(sketch, "E99.orphan", {"position": v(939.3, 74.97) * mm});
            skLineSegment(sketch, "E100", {"start": v(-212.8, 14.97) * mm, "end": v(-219.36, 14.97) * mm});
            skLineSegment(sketch, "E101", {"start": v(-212.8, -5.03) * mm, "end": v(-219.36, -5.03) * mm});
            skLineSegment(sketch, "E102", {"start": v(-191.7, -25.03) * mm, "end": v(-170.6, -25.03) * mm});
            skLineSegment(sketch, "E103.0.1.0", {"start": v(-212.8, 34.97) * mm, "end": v(-219.36, 34.97) * mm});
            skLineSegment(sketch, "E103.0.2.0", {"start": v(-212.8, 54.97) * mm, "end": v(-219.36, 54.97) * mm});
            skLineSegment(sketch, "E103.direction1", {"start": v(-219.36, 14.97) * mm, "end": v(-194.36, 14.97) * mm, "construction": true});
            skLineSegment(sketch, "E103.direction2", {"start": v(-219.36, 14.97) * mm, "end": v(-219.36, 34.97) * mm, "construction": true});
            skLineSegment(sketch, "E104.trimOffspring", {"start": v(-212.8, 54.97) * mm, "end": v(-212.8, 34.97) * mm});
            skLineSegment(sketch, "E105.trimOffspring", {"start": v(-219.36, 34.97) * mm, "end": v(-219.36, 14.97) * mm});
            skLineSegment(sketch, "E106.trimOffspring", {"start": v(-212.8, 14.97) * mm, "end": v(-212.8, -5.03) * mm});
            skLineSegment(sketch, "E107", {"start": v(-212.8, -25.03) * mm, "end": v(-219.36, -25.03) * mm});
            skLineSegment(sketch, "E108.trimOffspring", {"start": v(-219.36, -5.03) * mm, "end": v(-219.36, -25.03) * mm});
            skLineSegment(sketch, "E109.trimOffspring", {"start": v(-212.8, -25.03) * mm, "end": v(-212.8, -31.38) * mm});
            skLineSegment(sketch, "E110.MirrorCS", {"start": v(110.24, 14.97) * mm, "end": v(110.24, 34.97) * mm});
            skLineSegment(sketch, "E111.MirrorCS", {"start": v(110.24, -5.03) * mm, "end": v(110.24, -25.03) * mm});
            skLineSegment(sketch, "E112.MirrorCS", {"start": v(110.24, 34.97) * mm, "end": v(110.24, 14.97) * mm});
            skLineSegment(sketch, "E113.MirrorCS", {"start": v(103.7, 14.97) * mm, "end": v(103.7, -5.03) * mm});
            skLineSegment(sketch, "E114.MirrorCS", {"start": v(104.1, -25.03) * mm, "end": v(110.24, -25.03) * mm});
            skLineSegment(sketch, "E115.MirrorCS", {"start": v(103.7, 54.97) * mm, "end": v(103.7, 34.97) * mm});
            skLineSegment(sketch, "E116.MirrorCS", {"start": v(103.7, 34.97) * mm, "end": v(110.24, 34.97) * mm});
            skLineSegment(sketch, "E117.MirrorCS", {"start": v(103.7, 54.97) * mm, "end": v(110.24, 54.97) * mm});
            skLineSegment(sketch, "E118.MirrorCS", {"start": v(104.1, -25.03) * mm, "end": v(104.1, -31.38) * mm});
            skLineSegment(sketch, "E119.MirrorCS", {"start": v(103.7, 14.97) * mm, "end": v(110.24, 14.97) * mm});
            skLineSegment(sketch, "E120.MirrorCS", {"start": v(103.7, -5.03) * mm, "end": v(110.24, -5.03) * mm});
            skLineSegment(sketch, "E121.trimOffspring", {"start": v(103.9, 74.97) * mm, "end": v(110.24, 74.97) * mm});
            skLineSegment(sketch, "E122.MirrorCS", {"start": v(110.44, 74.97) * mm, "end": v(103.9, 74.97) * mm});
            skLineSegment(sketch, "E123.MirrorCS", {"start": v(103.9, 118.62) * mm, "end": v(103.9, 74.97) * mm});
            skPoint(sketch, "E124.orphan", {"position": v(110.24, 118.62) * mm});
            skPoint(sketch, "E125.orphan", {"position": v(-219.36, 118.62) * mm});
            skLineSegment(sketch, "E126", {"start": v(-191.7, -25.03) * mm, "end": v(-191.7, -31.38) * mm});
            skLineSegment(sketch, "E127.1.0.0", {"start": v(-170.6, -25.03) * mm, "end": v(-170.6, -31.38) * mm});
            skLineSegment(sketch, "E127.2.0.0", {"start": v(-149.5, -25.03) * mm, "end": v(-149.5, -31.38) * mm});
            skLineSegment(sketch, "E127.3.0.0", {"start": v(-128.4, -25.03) * mm, "end": v(-128.4, -31.38) * mm});
            skLineSegment(sketch, "E127.4.0.0", {"start": v(-107.3, -25.03) * mm, "end": v(-107.3, -31.38) * mm});
            skLineSegment(sketch, "E127.5.0.0", {"start": v(-86.2, -25.03) * mm, "end": v(-86.2, -31.38) * mm});
            skLineSegment(sketch, "E128", {"start": v(-86.2, -31.38) * mm, "end": v(-65.1, -31.38) * mm});
            skLineSegment(sketch, "E129", {"start": v(-149.5, -25.03) * mm, "end": v(-128.4, -25.03) * mm});
            skLineSegment(sketch, "E130", {"start": v(-107.3, -25.03) * mm, "end": v(-86.2, -25.03) * mm});
            skLineSegment(sketch, "E131", {"start": v(-128.4, -31.38) * mm, "end": v(-107.3, -31.38) * mm});
            skPoint(sketch, "E132.MirrorCS.end.orphan", {"position": v(-219.36, 112.27) * mm});
            skLineSegment(sketch, "E133.0.6.0", {"start": v(-65.1, -25.03) * mm, "end": v(-65.1, -31.38) * mm});
            skLineSegment(sketch, "E133.0.7.0", {"start": v(-44, -25.03) * mm, "end": v(-44, -31.38) * mm});
            skLineSegment(sketch, "E133.0.8.0", {"start": v(-22.9, -25.03) * mm, "end": v(-22.9, -31.38) * mm});
            skLineSegment(sketch, "E133.0.9.0", {"start": v(-1.8, -25.03) * mm, "end": v(-1.8, -31.38) * mm});
            skLineSegment(sketch, "E133.0.10.0", {"start": v(19.3, -25.03) * mm, "end": v(19.3, -31.38) * mm});
            skLineSegment(sketch, "E133.0.11.0", {"start": v(40.4, -25.03) * mm, "end": v(40.4, -31.38) * mm});
            skLineSegment(sketch, "E134.0.12.0", {"start": v(61.5, -25.03) * mm, "end": v(61.5, -31.38) * mm});
            skLineSegment(sketch, "E134.0.13.0", {"start": v(82.6, -25.03) * mm, "end": v(82.6, -31.38) * mm});
            skLineSegment(sketch, "E135", {"start": v(-65.1, -25.03) * mm, "end": v(-44, -25.03) * mm});
            skLineSegment(sketch, "E136.trimOffspring", {"start": v(-44, -31.38) * mm, "end": v(-22.9, -31.38) * mm});
            skLineSegment(sketch, "E137.trimOffspring", {"start": v(-22.9, -25.03) * mm, "end": v(-1.8, -25.03) * mm});
            skLineSegment(sketch, "E138.trimOffspring", {"start": v(-1.8, -31.38) * mm, "end": v(19.3, -31.38) * mm});
            skLineSegment(sketch, "E139.trimOffspring", {"start": v(19.3, -25.03) * mm, "end": v(40.4, -25.03) * mm});
            skLineSegment(sketch, "E140.trimOffspring", {"start": v(40.4, -31.38) * mm, "end": v(61.5, -31.38) * mm});
            skLineSegment(sketch, "E141.trimOffspring", {"start": v(61.5, -25.03) * mm, "end": v(82.6, -25.03) * mm});
            skLineSegment(sketch, "E142.trimOffspring", {"start": v(82.6, -31.38) * mm, "end": v(104.1, -31.38) * mm});
            skLineSegment(sketch, "E143.MirrorCS", {"start": v(82.6, 112.27) * mm, "end": v(82.6, 118.62) * mm});
            skLineSegment(sketch, "E144.MirrorCS", {"start": v(-86.2, 112.27) * mm, "end": v(-86.2, 118.62) * mm});
            skLineSegment(sketch, "E145.MirrorCS", {"start": v(-22.9, 112.27) * mm, "end": v(-22.9, 118.62) * mm});
            skLineSegment(sketch, "E146.MirrorCS", {"start": v(-149.5, 112.27) * mm, "end": v(-149.5, 118.62) * mm});
            skLineSegment(sketch, "E147.MirrorCS", {"start": v(-44, 112.27) * mm, "end": v(-44, 118.62) * mm});
            skLineSegment(sketch, "E148.MirrorCS", {"start": v(40.4, 112.27) * mm, "end": v(40.4, 118.62) * mm});
            skLineSegment(sketch, "E149.MirrorCS", {"start": v(19.3, 112.27) * mm, "end": v(19.3, 118.62) * mm});
            skLineSegment(sketch, "E150.MirrorCS", {"start": v(-65.1, 112.27) * mm, "end": v(-65.1, 118.62) * mm});
            skLineSegment(sketch, "E151.MirrorCS", {"start": v(-1.8, 112.27) * mm, "end": v(-1.8, 118.62) * mm});
            skLineSegment(sketch, "E152.MirrorCS", {"start": v(-191.7, 112.27) * mm, "end": v(-191.7, 118.62) * mm});
            skLineSegment(sketch, "E153.MirrorCS", {"start": v(-107.3, 112.27) * mm, "end": v(-107.3, 118.62) * mm});
            skLineSegment(sketch, "E154.MirrorCS", {"start": v(61.5, 112.27) * mm, "end": v(61.5, 118.62) * mm});
            skLineSegment(sketch, "E155.MirrorCS", {"start": v(-128.4, 112.27) * mm, "end": v(-128.4, 118.62) * mm});
            skLineSegment(sketch, "E156.MirrorCS", {"start": v(-170.6, 112.27) * mm, "end": v(-170.6, 118.62) * mm});
            skLineSegment(sketch, "E157.MirrorCS", {"start": v(-44, 118.62) * mm, "end": v(-22.9, 118.62) * mm});
            skLineSegment(sketch, "E158.MirrorCS", {"start": v(-107.3, 112.27) * mm, "end": v(-86.2, 112.27) * mm});
            skLineSegment(sketch, "E159.MirrorCS", {"start": v(-170.6, 118.62) * mm, "end": v(-149.5, 118.62) * mm});
            skLineSegment(sketch, "E160.MirrorCS", {"start": v(40.4, 118.62) * mm, "end": v(61.5, 118.62) * mm});
            skLineSegment(sketch, "E161.MirrorCS", {"start": v(-149.5, 112.27) * mm, "end": v(-128.4, 112.27) * mm});
            skLineSegment(sketch, "E162.MirrorCS", {"start": v(-65.1, 112.27) * mm, "end": v(-44, 112.27) * mm});
            skLineSegment(sketch, "E163.MirrorCS", {"start": v(-191.7, 112.27) * mm, "end": v(-170.6, 112.27) * mm});
            skLineSegment(sketch, "E164.MirrorCS", {"start": v(-22.9, 112.27) * mm, "end": v(-1.8, 112.27) * mm});
            skLineSegment(sketch, "E165.MirrorCS", {"start": v(-1.8, 118.62) * mm, "end": v(19.3, 118.62) * mm});
            skLineSegment(sketch, "E166.MirrorCS", {"start": v(-128.4, 118.62) * mm, "end": v(-107.3, 118.62) * mm});
            skLineSegment(sketch, "E167.MirrorCS", {"start": v(61.5, 112.27) * mm, "end": v(82.6, 112.27) * mm});
            skLineSegment(sketch, "E168.MirrorCS", {"start": v(19.3, 112.27) * mm, "end": v(40.4, 112.27) * mm});
            skLineSegment(sketch, "E169.MirrorCS", {"start": v(-86.2, 118.62) * mm, "end": v(-65.1, 118.62) * mm});
            skLineSegment(sketch, "E170.MirrorCS", {"start": v(82.6, 118.62) * mm, "end": v(104.1, 118.62) * mm});
            skLineSegment(sketch, "E171", {"start": v(-170.6, -31.38) * mm, "end": v(-149.5, -31.38) * mm});
            skSolve(sketch);
        }
        {
            var Q0;
            Q0=makeQuery(id+"F12.imprint","IMPRINT",FACE,{"disambiguationData":[TD([[makeQuery(id+"F12.imprint","IMPRINT",EDGE,{"derivedFrom":sQuery(id+"F12.wireOp",EDGE,"E93.top")}),1.0]])]});
            extrude(context, id + "F13", {"entities" : qUnion([Q0]), "depth" : 6.35 * mm});
        }
        {
            var Q0;
            Q0=makeQuery(id+"F1.opExtrude","CAP_FACE",FACE,{"disambiguationData":[OSD([sQuery(id+"F0.wireOp",EDGE,"E0.bottom"),sQuery(id+"F0.wireOp",EDGE,"E0.top"),sQuery(id+"F0.wireOp",EDGE,"E0.left"),sQuery(id+"F0.wireOp",EDGE,"E0.right"),sQuery(id+"F0.wireOp",EDGE,"E1.bottom"),sQuery(id+"F0.wireOp",EDGE,"E1.top"),sQuery(id+"F0.wireOp",EDGE,"E1.left"),sQuery(id+"F0.wireOp",EDGE,"E1.right"),sQuery(id+"F0.wireOp",EDGE,"E2.1.0.0"),sQuery(id+"F0.wireOp",EDGE,"E2.1.0.1"),sQuery(id+"F0.wireOp",EDGE,"E2.1.0.2"),sQuery(id+"F0.wireOp",EDGE,"E2.1.0.3"),sQuery(id+"F0.wireOp",EDGE,"E2.2.0.0"),sQuery(id+"F0.wireOp",EDGE,"E2.2.0.1"),sQuery(id+"F0.wireOp",EDGE,"E2.2.0.2"),sQuery(id+"F0.wireOp",EDGE,"E2.2.0.3"),sQuery(id+"F0.wireOp",EDGE,"E2.3.0.0"),sQuery(id+"F0.wireOp",EDGE,"E2.3.0.1"),sQuery(id+"F0.wireOp",EDGE,"E2.3.0.2"),sQuery(id+"F0.wireOp",EDGE,"E2.3.0.3"),sQuery(id+"F0.wireOp",EDGE,"E2.4.0.0"),sQuery(id+"F0.wireOp",EDGE,"E2.4.0.1"),sQuery(id+"F0.wireOp",EDGE,"E2.4.0.2"),sQuery(id+"F0.wireOp",EDGE,"E2.4.0.3"),sQuery(id+"F0.wireOp",EDGE,"E2.5.0.0"),sQuery(id+"F0.wireOp",EDGE,"E2.5.0.1"),sQuery(id+"F0.wireOp",EDGE,"E2.5.0.2"),sQuery(id+"F0.wireOp",EDGE,"E2.5.0.3"),sQuery(id+"F0.wireOp",EDGE,"E2.6.0.0"),sQuery(id+"F0.wireOp",EDGE,"E2.6.0.1"),sQuery(id+"F0.wireOp",EDGE,"E2.6.0.2"),sQuery(id+"F0.wireOp",EDGE,"E2.6.0.3"),sQuery(id+"F0.wireOp",EDGE,"E2.7.0.0"),sQuery(id+"F0.wireOp",EDGE,"E2.7.0.1"),sQuery(id+"F0.wireOp",EDGE,"E2.7.0.2"),sQuery(id+"F0.wireOp",EDGE,"E2.7.0.3"),sQuery(id+"F0.wireOp",EDGE,"E3.top"),sQuery(id+"F0.wireOp",EDGE,"E3.right"),sQuery(id+"F0.wireOp",EDGE,"E3.bottom"),sQuery(id+"F0.wireOp",EDGE,"E3.left"),sQuery(id+"F0.wireOp",EDGE,"E4.top"),sQuery(id+"F0.wireOp",EDGE,"E4.left"),sQuery(id+"F0.wireOp",EDGE,"E4.bottom"),sQuery(id+"F0.wireOp",EDGE,"E4.right")])],"isStart":false});
            var sketch = newSketch(context, id + "F14", { "sketchPlane" : qUnion([Q0])});
            skLineSegment(sketch, "E172.top", {"start": v(154.98, -341.11) * mm, "end": v(176.08, -341.11) * mm});
            skLineSegment(sketch, "E172.left", {"start": v(148.43, -74.76) * mm, "end": v(148.43, -94.76) * mm});
            skLineSegment(sketch, "E172.right", {"start": v(478.03, -74.76) * mm, "end": v(478.03, -94.76) * mm});
            skPoint(sketch, "E173.orphan", {"position": v(-196.96, 42.53) * mm});
            skPoint(sketch, "E174.orphan", {"position": v(1301.59, 42.53) * mm});
            skLineSegment(sketch, "E175", {"start": v(176.08, -334.76) * mm, "end": v(197.18, -334.76) * mm});
            skLineSegment(sketch, "E176.direction2", {"start": v(148.43, -134.76) * mm, "end": v(148.43, -114.76) * mm, "construction": true});
            skLineSegment(sketch, "E177.trimOffspring", {"start": v(154.98, -94.76) * mm, "end": v(154.98, -114.76) * mm});
            skLineSegment(sketch, "E178.trimOffspring", {"start": v(148.43, -114.76) * mm, "end": v(148.43, -134.76) * mm});
            skLineSegment(sketch, "E179.trimOffspring", {"start": v(154.98, -134.76) * mm, "end": v(154.98, -154.76) * mm});
            skLineSegment(sketch, "E180", {"start": v(154.98, -334.76) * mm, "end": v(148.43, -334.76) * mm});
            skLineSegment(sketch, "E181.trimOffspring", {"start": v(148.43, -154.76) * mm, "end": v(148.43, -174.76) * mm});
            skLineSegment(sketch, "E182.trimOffspring", {"start": v(154.98, -334.76) * mm, "end": v(154.98, -341.11) * mm});
            skLineSegment(sketch, "E183.MirrorCS", {"start": v(478.03, -134.76) * mm, "end": v(478.03, -114.76) * mm});
            skLineSegment(sketch, "E184.MirrorCS", {"start": v(478.03, -114.76) * mm, "end": v(478.03, -134.76) * mm});
            skLineSegment(sketch, "E185.MirrorCS", {"start": v(471.48, -134.76) * mm, "end": v(471.48, -154.76) * mm});
            skLineSegment(sketch, "E186.MirrorCS", {"start": v(471.88, -334.76) * mm, "end": v(478.03, -334.76) * mm});
            skLineSegment(sketch, "E187.MirrorCS", {"start": v(471.48, -94.76) * mm, "end": v(471.48, -114.76) * mm});
            skLineSegment(sketch, "E188.MirrorCS", {"start": v(471.88, -334.76) * mm, "end": v(471.88, -341.11) * mm});
            skLineSegment(sketch, "E189.MirrorCS", {"start": v(471.68, -31.11) * mm, "end": v(471.68, -74.76) * mm});
            skLineSegment(sketch, "E190", {"start": v(176.08, -334.76) * mm, "end": v(176.08, -341.11) * mm});
            skLineSegment(sketch, "E191.1.0.0", {"start": v(197.18, -334.76) * mm, "end": v(197.18, -341.11) * mm});
            skLineSegment(sketch, "E191.2.0.0", {"start": v(218.28, -334.76) * mm, "end": v(218.28, -341.11) * mm});
            skLineSegment(sketch, "E191.3.0.0", {"start": v(239.38, -334.76) * mm, "end": v(239.38, -341.11) * mm});
            skLineSegment(sketch, "E191.4.0.0", {"start": v(260.48, -334.76) * mm, "end": v(260.48, -341.11) * mm});
            skLineSegment(sketch, "E191.5.0.0", {"start": v(281.58, -334.76) * mm, "end": v(281.58, -341.11) * mm});
            skLineSegment(sketch, "E192", {"start": v(281.58, -341.11) * mm, "end": v(302.68, -341.11) * mm});
            skLineSegment(sketch, "E193", {"start": v(218.28, -334.76) * mm, "end": v(239.38, -334.76) * mm});
            skLineSegment(sketch, "E194", {"start": v(260.48, -334.76) * mm, "end": v(281.58, -334.76) * mm});
            skLineSegment(sketch, "E195", {"start": v(239.38, -341.11) * mm, "end": v(260.48, -341.11) * mm});
            skLineSegment(sketch, "E196.0.6.0", {"start": v(302.68, -334.76) * mm, "end": v(302.68, -341.11) * mm});
            skLineSegment(sketch, "E196.0.7.0", {"start": v(323.78, -334.76) * mm, "end": v(323.78, -341.11) * mm});
            skLineSegment(sketch, "E196.0.8.0", {"start": v(344.88, -334.76) * mm, "end": v(344.88, -341.11) * mm});
            skLineSegment(sketch, "E196.0.9.0", {"start": v(365.98, -334.76) * mm, "end": v(365.98, -341.11) * mm});
            skLineSegment(sketch, "E196.0.10.0", {"start": v(387.08, -334.76) * mm, "end": v(387.08, -341.11) * mm});
            skLineSegment(sketch, "E196.0.11.0", {"start": v(408.18, -334.76) * mm, "end": v(408.18, -341.11) * mm});
            skLineSegment(sketch, "E197.0.12.0", {"start": v(429.28, -334.76) * mm, "end": v(429.28, -341.11) * mm});
            skLineSegment(sketch, "E197.0.13.0", {"start": v(450.38, -334.76) * mm, "end": v(450.38, -341.11) * mm});
            skLineSegment(sketch, "E198", {"start": v(302.68, -334.76) * mm, "end": v(323.78, -334.76) * mm});
            skLineSegment(sketch, "E199.trimOffspring", {"start": v(323.78, -341.11) * mm, "end": v(344.88, -341.11) * mm});
            skLineSegment(sketch, "E200.trimOffspring", {"start": v(344.88, -334.76) * mm, "end": v(365.98, -334.76) * mm});
            skLineSegment(sketch, "E201.trimOffspring", {"start": v(365.98, -341.11) * mm, "end": v(387.08, -341.11) * mm});
            skLineSegment(sketch, "E202.trimOffspring", {"start": v(387.08, -334.76) * mm, "end": v(408.18, -334.76) * mm});
            skLineSegment(sketch, "E203.trimOffspring", {"start": v(408.18, -341.11) * mm, "end": v(429.28, -341.11) * mm});
            skLineSegment(sketch, "E204.trimOffspring", {"start": v(429.28, -334.76) * mm, "end": v(450.38, -334.76) * mm});
            skLineSegment(sketch, "E205.trimOffspring", {"start": v(450.38, -341.11) * mm, "end": v(471.88, -341.11) * mm});
            skLineSegment(sketch, "E206.MirrorCS", {"start": v(450.38, -37.46) * mm, "end": v(450.38, -31.11) * mm});
            skLineSegment(sketch, "E207.MirrorCS", {"start": v(281.58, -37.46) * mm, "end": v(281.58, -31.11) * mm});
            skLineSegment(sketch, "E208.MirrorCS", {"start": v(344.88, -37.46) * mm, "end": v(344.88, -31.11) * mm});
            skLineSegment(sketch, "E209.MirrorCS", {"start": v(218.28, -37.46) * mm, "end": v(218.28, -31.11) * mm});
            skLineSegment(sketch, "E210.MirrorCS", {"start": v(323.78, -37.46) * mm, "end": v(323.78, -31.11) * mm});
            skLineSegment(sketch, "E211.MirrorCS", {"start": v(408.18, -37.46) * mm, "end": v(408.18, -31.11) * mm});
            skLineSegment(sketch, "E212.MirrorCS", {"start": v(387.08, -37.46) * mm, "end": v(387.08, -31.11) * mm});
            skLineSegment(sketch, "E213.MirrorCS", {"start": v(302.68, -37.46) * mm, "end": v(302.68, -31.11) * mm});
            skLineSegment(sketch, "E214.MirrorCS", {"start": v(365.98, -37.46) * mm, "end": v(365.98, -31.11) * mm});
            skLineSegment(sketch, "E215.MirrorCS", {"start": v(176.08, -37.46) * mm, "end": v(176.08, -31.11) * mm});
            skLineSegment(sketch, "E216.MirrorCS", {"start": v(260.48, -37.46) * mm, "end": v(260.48, -31.11) * mm});
            skLineSegment(sketch, "E217.MirrorCS", {"start": v(429.28, -37.46) * mm, "end": v(429.28, -31.11) * mm});
            skLineSegment(sketch, "E218.MirrorCS", {"start": v(239.38, -37.46) * mm, "end": v(239.38, -31.11) * mm});
            skLineSegment(sketch, "E219.MirrorCS", {"start": v(197.18, -37.46) * mm, "end": v(197.18, -31.11) * mm});
            skLineSegment(sketch, "E220.MirrorCS", {"start": v(323.78, -31.11) * mm, "end": v(344.88, -31.11) * mm});
            skLineSegment(sketch, "E221.MirrorCS", {"start": v(260.48, -37.46) * mm, "end": v(281.58, -37.46) * mm});
            skLineSegment(sketch, "E222.MirrorCS", {"start": v(197.18, -31.11) * mm, "end": v(218.28, -31.11) * mm});
            skLineSegment(sketch, "E223.MirrorCS", {"start": v(408.18, -31.11) * mm, "end": v(429.28, -31.11) * mm});
            skLineSegment(sketch, "E224.MirrorCS", {"start": v(218.28, -37.46) * mm, "end": v(239.38, -37.46) * mm});
            skLineSegment(sketch, "E225.MirrorCS", {"start": v(302.68, -37.46) * mm, "end": v(323.78, -37.46) * mm});
            skLineSegment(sketch, "E226.MirrorCS", {"start": v(176.08, -37.46) * mm, "end": v(197.18, -37.46) * mm});
            skLineSegment(sketch, "E227.MirrorCS", {"start": v(344.88, -37.46) * mm, "end": v(365.98, -37.46) * mm});
            skLineSegment(sketch, "E228.MirrorCS", {"start": v(365.98, -31.11) * mm, "end": v(387.08, -31.11) * mm});
            skLineSegment(sketch, "E229.MirrorCS", {"start": v(239.38, -31.11) * mm, "end": v(260.48, -31.11) * mm});
            skLineSegment(sketch, "E230.MirrorCS", {"start": v(429.28, -37.46) * mm, "end": v(450.38, -37.46) * mm});
            skLineSegment(sketch, "E231.MirrorCS", {"start": v(387.08, -37.46) * mm, "end": v(408.18, -37.46) * mm});
            skLineSegment(sketch, "E232.MirrorCS", {"start": v(281.58, -31.11) * mm, "end": v(302.68, -31.11) * mm});
            skLineSegment(sketch, "E233.MirrorCS", {"start": v(450.38, -31.11) * mm, "end": v(471.88, -31.11) * mm});
            skLineSegment(sketch, "E234", {"start": v(197.18, -341.11) * mm, "end": v(218.28, -341.11) * mm});
            skLineSegment(sketch, "E235", {"start": v(478.03, -94.76) * mm, "end": v(471.48, -94.76) * mm});
            skLineSegment(sketch, "E236", {"start": v(478.03, -114.76) * mm, "end": v(471.48, -114.76) * mm});
            skLineSegment(sketch, "E237", {"start": v(478.03, -134.76) * mm, "end": v(471.48, -134.76) * mm});
            skLineSegment(sketch, "E238", {"start": v(478.03, -154.76) * mm, "end": v(471.48, -154.76) * mm});
            skLineSegment(sketch, "E239", {"start": v(478.03, -74.76) * mm, "end": v(471.68, -74.76) * mm});
            skLineSegment(sketch, "E240", {"start": v(148.43, -74.76) * mm, "end": v(154.98, -74.76) * mm});
            skLineSegment(sketch, "E241", {"start": v(154.98, -31.11) * mm, "end": v(154.98, -74.76) * mm});
            skLineSegment(sketch, "E242", {"start": v(176.08, -31.11) * mm, "end": v(154.98, -31.11) * mm});
            skLineSegment(sketch, "E243", {"start": v(154.98, -94.76) * mm, "end": v(148.43, -94.76) * mm});
            skLineSegment(sketch, "E244", {"start": v(154.98, -114.76) * mm, "end": v(148.43, -114.76) * mm});
            skLineSegment(sketch, "E245", {"start": v(154.98, -134.76) * mm, "end": v(148.43, -134.76) * mm});
            skLineSegment(sketch, "E246", {"start": v(154.98, -154.76) * mm, "end": v(148.43, -154.76) * mm});
            skLineSegment(sketch, "E247", {"start": v(148.43, -174.76) * mm, "end": v(154.98, -174.76) * mm});
            skLineSegment(sketch, "E248", {"start": v(478.03, -194.76) * mm, "end": v(471.48, -194.76) * mm});
            skLineSegment(sketch, "E249", {"start": v(478.03, -214.76) * mm, "end": v(471.48, -214.76) * mm});
            skLineSegment(sketch, "E250", {"start": v(478.03, -234.76) * mm, "end": v(471.48, -234.76) * mm});
            skLineSegment(sketch, "E251", {"start": v(478.03, -254.76) * mm, "end": v(471.48, -254.76) * mm});
            skLineSegment(sketch, "E252", {"start": v(478.03, -274.76) * mm, "end": v(471.48, -274.76) * mm});
            skLineSegment(sketch, "E253", {"start": v(148.43, -294.76) * mm, "end": v(154.98, -294.76) * mm});
            skLineSegment(sketch, "E254", {"start": v(471.48, -174.76) * mm, "end": v(471.48, -194.76) * mm});
            skLineSegment(sketch, "E255.trimOffspring", {"start": v(471.48, -214.76) * mm, "end": v(471.48, -234.76) * mm});
            skLineSegment(sketch, "E256.trimOffspring", {"start": v(471.48, -254.76) * mm, "end": v(471.48, -274.76) * mm});
            skLineSegment(sketch, "E257", {"start": v(148.43, -314.76) * mm, "end": v(154.98, -314.76) * mm});
            skLineSegment(sketch, "E258", {"start": v(471.48, -294.76) * mm, "end": v(471.48, -314.76) * mm});
            skLineSegment(sketch, "E259.trimOffspring", {"start": v(478.03, -314.76) * mm, "end": v(478.03, -334.76) * mm});
            skLineSegment(sketch, "E260.trimOffspring", {"start": v(478.03, -274.76) * mm, "end": v(478.03, -294.76) * mm});
            skLineSegment(sketch, "E261", {"start": v(154.98, -174.76) * mm, "end": v(154.98, -194.76) * mm});
            skLineSegment(sketch, "E262", {"start": v(478.03, -254.76) * mm, "end": v(478.03, -234.76) * mm});
            skLineSegment(sketch, "E263", {"start": v(478.03, -214.76) * mm, "end": v(478.03, -194.76) * mm});
            skLineSegment(sketch, "E264", {"start": v(478.03, -174.76) * mm, "end": v(478.03, -154.76) * mm});
            skLineSegment(sketch, "E265.trimOffspring", {"start": v(154.98, -214.76) * mm, "end": v(154.98, -234.76) * mm});
            skLineSegment(sketch, "E266.trimOffspring", {"start": v(154.98, -254.76) * mm, "end": v(154.98, -274.76) * mm});
            skLineSegment(sketch, "E267.trimOffspring", {"start": v(154.98, -294.76) * mm, "end": v(154.98, -314.76) * mm});
            skLineSegment(sketch, "E268.trimOffspring", {"start": v(148.43, -314.76) * mm, "end": v(148.43, -334.76) * mm});
            skLineSegment(sketch, "E269.trimOffspring", {"start": v(148.43, -274.76) * mm, "end": v(148.43, -294.76) * mm});
            skLineSegment(sketch, "E270.trimOffspring", {"start": v(148.43, -234.76) * mm, "end": v(148.43, -254.76) * mm});
            skLineSegment(sketch, "E271.trimOffspring", {"start": v(148.43, -194.76) * mm, "end": v(148.43, -214.76) * mm});
            skLineSegment(sketch, "E272.trimOffspring", {"start": v(471.48, -174.76) * mm, "end": v(478.03, -174.76) * mm});
            skLineSegment(sketch, "E273.trimOffspring", {"start": v(154.98, -194.76) * mm, "end": v(148.43, -194.76) * mm});
            skLineSegment(sketch, "E274.trimOffspring", {"start": v(154.98, -214.76) * mm, "end": v(148.43, -214.76) * mm});
            skLineSegment(sketch, "E275.trimOffspring", {"start": v(154.98, -234.76) * mm, "end": v(148.43, -234.76) * mm});
            skLineSegment(sketch, "E276.trimOffspring", {"start": v(154.98, -254.76) * mm, "end": v(148.43, -254.76) * mm});
            skLineSegment(sketch, "E277.trimOffspring", {"start": v(154.98, -274.76) * mm, "end": v(148.43, -274.76) * mm});
            skLineSegment(sketch, "E278.trimOffspring", {"start": v(471.48, -294.76) * mm, "end": v(478.03, -294.76) * mm});
            skLineSegment(sketch, "E279.trimOffspring", {"start": v(471.48, -314.76) * mm, "end": v(478.03, -314.76) * mm});
            skSolve(sketch);
        }
        {
            var Q0;
            Q0=makeQuery(id+"F14.imprint","IMPRINT",FACE,{"disambiguationData":[TD([[makeQuery(id+"F14.imprint","IMPRINT",EDGE,{"derivedFrom":sQuery(id+"F14.wireOp",EDGE,"E172.top")}),1.0]])]});
            extrude(context, id + "F15", {"entities" : qUnion([Q0]), "operationType" : NewBodyOperationType.ADD, "depth" : 6.35 * mm});
        }
    });
